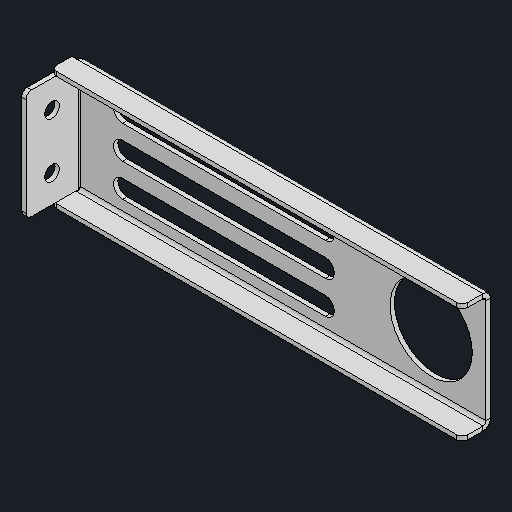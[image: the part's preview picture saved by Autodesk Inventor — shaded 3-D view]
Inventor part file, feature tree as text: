
AUTODESK INVENTOR PART (.ipt)
format: ipt  version: 2024.2 (Build 282272000, 272)  size: 129,024 bytes
history: native  units: mm
features: other x1, fillet x1
ambient origin geometry x8: Origin, YZ Plane, XZ Plane, XY Plane, X Axis, Y Axis, Z Axis, Center Point
bodies: Body1 (feature_tree)
feature tree (2):
  other  "솔리드1"
  fillet  "Fillet2"  [1 undecoded]
note: 1 required parameter value undecoded (feature->parameter linkage not recoverable at this tier; creation-order binding heuristic only, values carry confidence <= 0.55)
